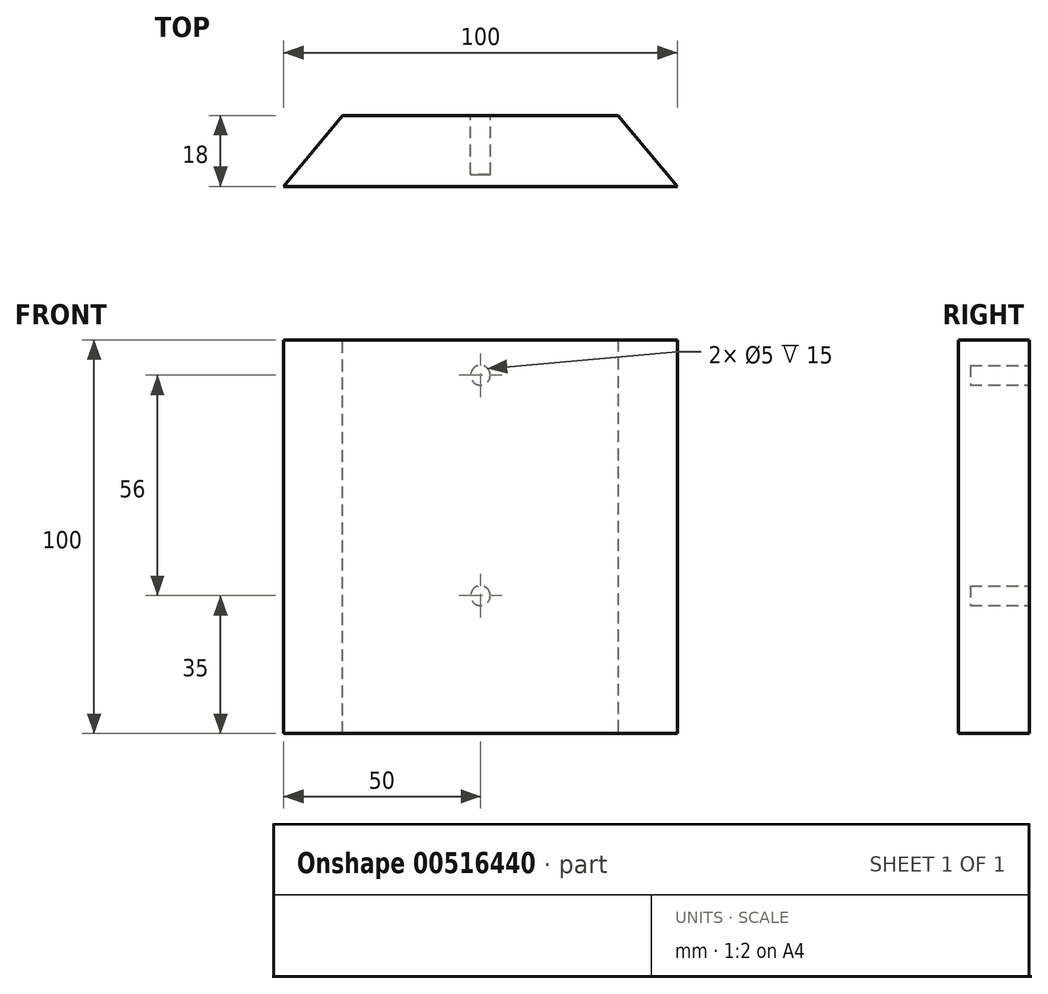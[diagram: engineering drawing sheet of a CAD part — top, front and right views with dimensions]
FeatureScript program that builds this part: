
annotation { "Feature Type Name" : "Feature", "Feature Type Description" : "" }
export const myFeature = defineFeature(function(context is Context, id is Id, definition is map)
    precondition{}
    {
        {
            var Q0;
            Q0=qCreatedBy(makeId("Front.planeOp"),FACE);
            var sketch = newSketch(context, id + "F0", { "sketchPlane" : qUnion([Q0])});
            skLineSegment(sketch, "E0.bottom", {"start": v(50, -50) * mm, "end": v(-50, -50) * mm});
            skLineSegment(sketch, "E0.top", {"start": v(50, 50) * mm, "end": v(-50, 50) * mm});
            skLineSegment(sketch, "E0.left", {"start": v(50, -50) * mm, "end": v(50, 50) * mm});
            skLineSegment(sketch, "E0.right", {"start": v(-50, -50) * mm, "end": v(-50, 50) * mm});
            skPoint(sketch, "E0.middle", {"position": v(0, 0) * mm});
            skSolve(sketch);
        }
        {
            var Q0;
            Q0 = qSketchRegion(id + "F0", true);
            extrude(context, id + "F1", {"entities" : qUnion([Q0]), "depth" : 18 * mm, "offsetDistance" : 25 * mm});
        }
        {
            var Q0;
            Q0=makeQuery(id+"F1.opExtrude","CAP_EDGE",EDGE,{"disambiguationData":[OSD([sQuery(id+"F0.wireOp",EDGE,"E0.left")])],"isStart":true});
            var Q1;
            Q1=makeQuery(id+"F1.opExtrude","CAP_EDGE",EDGE,{"disambiguationData":[OSD([sQuery(id+"F0.wireOp",EDGE,"E0.right")])],"isStart":true});
            chamfer(context, id + "F2", {"entities" : qUnion([Q0, Q1]), "chamferType" : ChamferType.TWO_OFFSETS, "width1" : 18 * mm, "oppositeDirection" : false, "width2" : 15 * mm, "tangentPropagation" : true});
        }
        {
            var Q0;
            Q0=makeQuery(id+"F1.opExtrude","CAP_FACE",FACE,{"disambiguationData":[OSD([sQuery(id+"F0.wireOp",EDGE,"E0.bottom"),sQuery(id+"F0.wireOp",EDGE,"E0.top"),sQuery(id+"F0.wireOp",EDGE,"E0.left"),sQuery(id+"F0.wireOp",EDGE,"E0.right")])],"isStart":true});
            var sketch = newSketch(context, id + "F3", { "sketchPlane" : qUnion([Q0])});
            skCircle(sketch, "E1", {"center": v(0, -15) * mm, "radius": 2.5 * mm});
            skCircle(sketch, "E2.0.1.0", {"center": v(0, 41) * mm, "radius": 2.5 * mm});
            skLineSegment(sketch, "E2.direction1", {"start": v(0, -15) * mm, "end": v(25, -15) * mm, "construction": true});
            skLineSegment(sketch, "E2.direction2", {"start": v(0, -15) * mm, "end": v(0, 41) * mm, "construction": true});
            skSolve(sketch);
        }
        {
            var Q0;
            Q0 = qSketchRegion(id + "F3", true);
            extrude(context, id + "F4", {"entities" : qUnion([Q0]), "operationType" : NewBodyOperationType.REMOVE, "oppositeDirection" : true, "depth" : 15 * mm, "offsetDistance" : 25 * mm});
        }
    });
